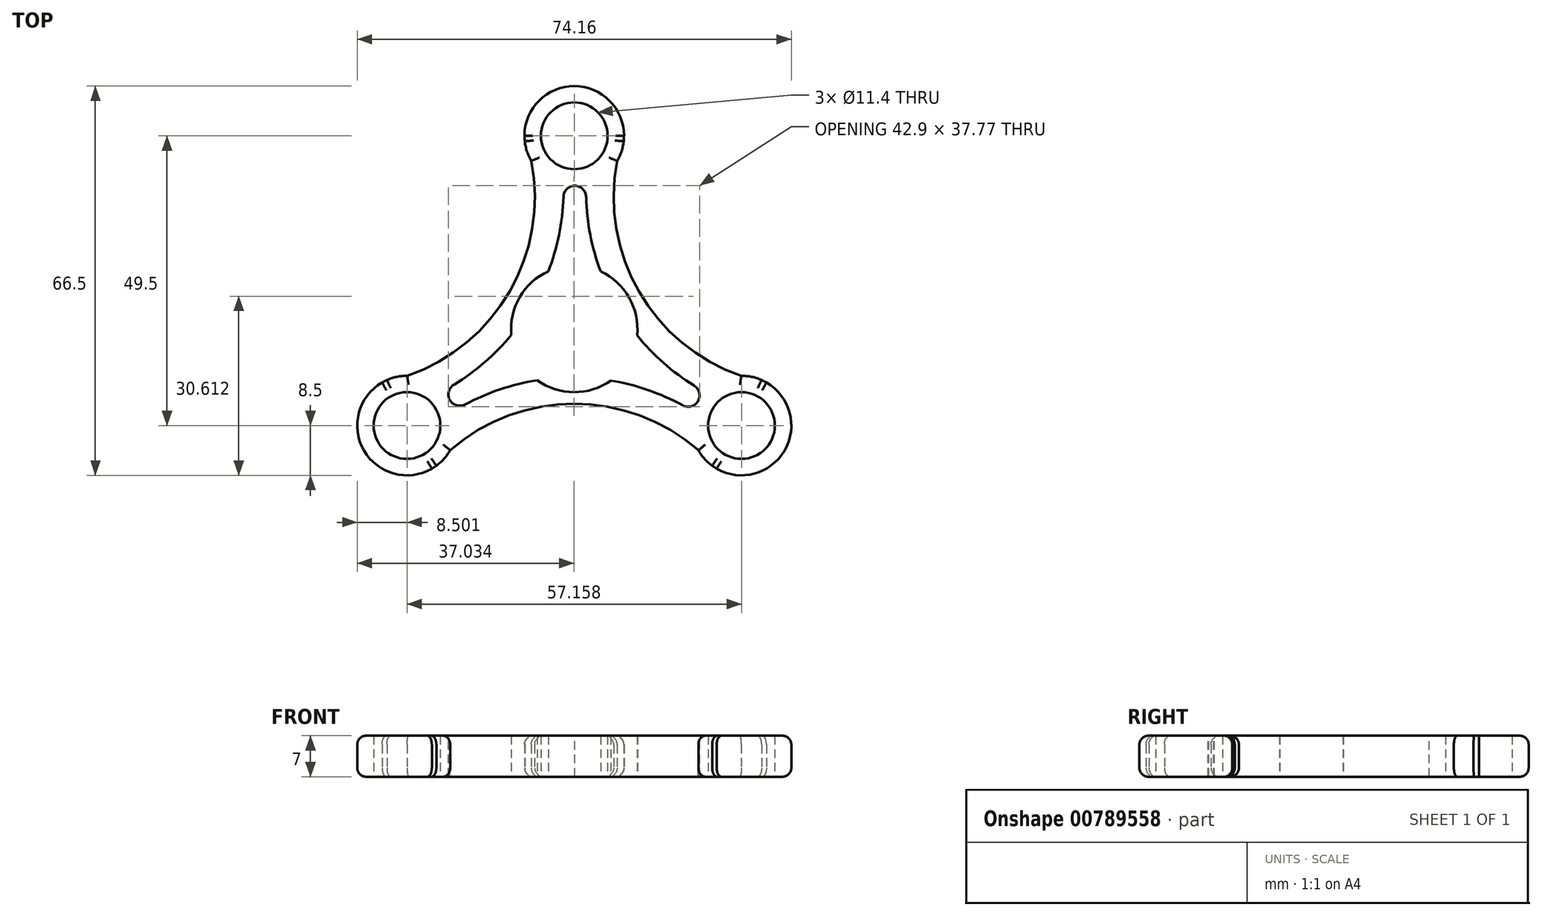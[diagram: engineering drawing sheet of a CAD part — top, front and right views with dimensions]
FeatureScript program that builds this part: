
annotation { "Feature Type Name" : "Feature", "Feature Type Description" : "" }
export const myFeature = defineFeature(function(context is Context, id is Id, definition is map)
    precondition{}
    {
        {
            var Q0;
            Q0=qCreatedBy(makeId("Top.planeOp"),FACE);
            var sketch = newSketch(context, id + "F0", { "sketchPlane" : qUnion([Q0])});
            skCircle(sketch, "E0", {"center": v(0, 0) * mm, "radius": 10.8 * mm});
            skCircle(sketch, "E1", {"center": v(0, 33) * mm, "radius": 5.7 * mm});
            skArc(sketch, "E2", {"start": v(7.35, 28.73) * mm, "mid": v(0, 41.5) * mm, "end": v(-7.35, 28.73) * mm});
            skCircle(sketch, "E3.1.0", {"center": v(-28.58, -16.5) * mm, "radius": 5.7 * mm});
            skArc(sketch, "E3.1.1", {"start": v(-28.55, -8) * mm, "mid": v(-35.94, -20.75) * mm, "end": v(-21.2, -20.73) * mm});
            skCircle(sketch, "E3.2.0", {"center": v(28.58, -16.5) * mm, "radius": 5.7 * mm});
            skArc(sketch, "E3.2.1", {"start": v(22.31, -10.76) * mm, "mid": v(21.17, -12.34) * mm, "end": v(20.41, -14.14) * mm});
            skLineSegment(sketch, "E4", {"start": v(0, 0) * mm, "end": v(28.58, -16.5) * mm, "construction": true});
            skLineSegment(sketch, "E5", {"start": v(28.58, -16.5) * mm, "end": v(38.1, 0) * mm, "construction": true});
            skArc(sketch, "E6", {"start": v(8.5, 33) * mm, "mid": v(8.47, 32.54) * mm, "end": v(8.45, 32.09) * mm});
            skArc(sketch, "E7.1.0", {"start": v(-32.83, -9.14) * mm, "mid": v(-32.42, -8.93) * mm, "end": v(-32.01, -8.72) * mm});
            skArc(sketch, "E7.2.0", {"start": v(24.33, -23.86) * mm, "mid": v(23.95, -23.6) * mm, "end": v(23.56, -23.36) * mm});
            skArc(sketch, "E8", {"start": v(2.04, 24.75) * mm, "mid": v(2.54, 17.16) * mm, "end": v(4.5, 9.81) * mm});
            skArc(sketch, "E9.trimOffspring", {"start": v(10.74, -1.1) * mm, "mid": v(16.06, -6.49) * mm, "end": v(22.31, -10.76) * mm});
            skArc(sketch, "E10.trimOffspring", {"start": v(-6.32, -8.76) * mm, "mid": v(-13.65, -10.66) * mm, "end": v(-20.47, -13.94) * mm});
            skArc(sketch, "E11.trimOffspring", {"start": v(-4.43, 9.85) * mm, "mid": v(-2.41, 17.15) * mm, "end": v(-1.84, 24.7) * mm});
            skArc(sketch, "E12.trimOffspring", {"start": v(32.01, -8.72) * mm, "mid": v(32.42, -8.93) * mm, "end": v(32.83, -9.14) * mm});
            skArc(sketch, "E13.trimOffspring", {"start": v(-23.56, -23.36) * mm, "mid": v(-23.95, -23.6) * mm, "end": v(-24.33, -23.86) * mm});
            skArc(sketch, "E14.trimOffspring", {"start": v(-8.45, 32.09) * mm, "mid": v(-8.47, 32.54) * mm, "end": v(-8.5, 33) * mm});
            skArc(sketch, "E15", {"start": v(7.35, 28.73) * mm, "mid": v(11.06, 6.38) * mm, "end": v(28.55, -8) * mm});
            skArc(sketch, "E16.1.0", {"start": v(-28.55, -8) * mm, "mid": v(-11.06, 6.38) * mm, "end": v(-7.35, 28.73) * mm});
            skArc(sketch, "E16.2.0", {"start": v(21.2, -20.73) * mm, "mid": v(0, -12.77) * mm, "end": v(-21.2, -20.73) * mm});
            skPoint(sketch, "E17.orphan", {"position": v(-2.9, 33) * mm});
            skPoint(sketch, "E18.orphan", {"position": v(3.18, 33) * mm});
            skArc(sketch, "E19.trimOffspring", {"start": v(-1.84, 24.7) * mm, "mid": v(0.1, 24.5) * mm, "end": v(2.04, 24.75) * mm});
            skPoint(sketch, "E20.orphan", {"position": v(-8.5, 33) * mm});
            skArc(sketch, "E21.trimOffspring", {"start": v(20.41, -14.14) * mm, "mid": v(13.59, -10.78) * mm, "end": v(6.25, -8.81) * mm});
            skArc(sketch, "E22.trimOffspring", {"start": v(21.2, -20.73) * mm, "mid": v(35.94, -20.75) * mm, "end": v(28.55, -8) * mm});
            skPoint(sketch, "E23.orphan", {"position": v(24.33, -23.86) * mm});
            skArc(sketch, "E24.trimOffspring", {"start": v(-22.45, -10.6) * mm, "mid": v(-16.13, -6.38) * mm, "end": v(-10.75, -1) * mm});
            skArc(sketch, "E25.trimOffspring", {"start": v(-20.47, -13.94) * mm, "mid": v(-21.27, -12.16) * mm, "end": v(-22.45, -10.6) * mm});
            skPoint(sketch, "E26.orphan", {"position": v(-32.83, -9.14) * mm});
            skPoint(sketch, "E27.orphan", {"position": v(-24.33, -23.86) * mm});
            skSolve(sketch);
        }
        {
            var Q0;
            Q0=makeQuery(id+"F0.imprint","IMPRINT",FACE,{"disambiguationData":[TD([[makeQuery(id+"F0.imprint","IMPRINT",EDGE,{"derivedFrom":sQuery(id+"F0.wireOp",EDGE,"E1")}),-1.0]])]});
            extrude(context, id + "F1", {"entities" : qUnion([Q0]), "depth" : 7 * mm, "offsetDistance" : 25 * mm});
        }
        {
            var Q0;
            Q0=makeQuery(id+"F1.opExtrude","SWEPT_EDGE",EDGE,{"disambiguationData":[OSD([sQuery(id+"F0.wireOp",EDGE,"E11.trimOffspring"),sQuery(id+"F0.wireOp",EDGE,"E19.trimOffspring")])]});
            var Q1;
            Q1=makeQuery(id+"F1.opExtrude","SWEPT_EDGE",EDGE,{"disambiguationData":[OSD([sQuery(id+"F0.wireOp",EDGE,"E8"),sQuery(id+"F0.wireOp",EDGE,"E19.trimOffspring")])]});
            var Q2;
            Q2=makeQuery(id+"F1.opExtrude","SWEPT_EDGE",EDGE,{"disambiguationData":[OSD([sQuery(id+"F0.wireOp",EDGE,"E3.2.1"),sQuery(id+"F0.wireOp",EDGE,"E9.trimOffspring")])]});
            var Q3;
            Q3=makeQuery(id+"F1.opExtrude","SWEPT_EDGE",EDGE,{"disambiguationData":[OSD([sQuery(id+"F0.wireOp",EDGE,"E3.2.1"),sQuery(id+"F0.wireOp",EDGE,"E21.trimOffspring")])]});
            var Q4;
            Q4=makeQuery(id+"F1.opExtrude","SWEPT_EDGE",EDGE,{"disambiguationData":[OSD([sQuery(id+"F0.wireOp",EDGE,"E10.trimOffspring"),sQuery(id+"F0.wireOp",EDGE,"E25.trimOffspring")])]});
            var Q5;
            Q5=makeQuery(id+"F1.opExtrude","SWEPT_EDGE",EDGE,{"disambiguationData":[OSD([sQuery(id+"F0.wireOp",EDGE,"E24.trimOffspring"),sQuery(id+"F0.wireOp",EDGE,"E25.trimOffspring")])]});
            fillet(context, id + "F2", {"entities" : qUnion([Q0, Q1, Q2, Q3, Q4, Q5]), "radius" : 2 * mm, "tangentPropagation" : true, "allowEdgeOverflow" : false});
        }
        {
            var Q0;
            Q0=makeQuery(id+"F1.opExtrude","CAP_EDGE",EDGE,{"disambiguationData":[OSD([sQuery(id+"F0.wireOp",EDGE,"E16.2.0")])],"isStart":false});
            var Q1;
            Q1=makeQuery(id+"F1.opExtrude","CAP_EDGE",EDGE,{"disambiguationData":[OSD([sQuery(id+"F0.wireOp",EDGE,"E15")])],"isStart":false});
            var Q2;
            Q2=makeQuery(id+"F1.opExtrude","CAP_EDGE",EDGE,{"disambiguationData":[OSD([sQuery(id+"F0.wireOp",EDGE,"E16.1.0")])],"isStart":false});
            var Q3;
            Q3=makeQuery(id+"F1.opExtrude","CAP_EDGE",EDGE,{"disambiguationData":[OSD([sQuery(id+"F0.wireOp",EDGE,"E16.2.0")])],"isStart":true});
            var Q4;
            Q4=makeQuery(id+"F1.opExtrude","CAP_EDGE",EDGE,{"disambiguationData":[OSD([sQuery(id+"F0.wireOp",EDGE,"E15")])],"isStart":true});
            var Q5;
            Q5=makeQuery(id+"F1.opExtrude","CAP_EDGE",EDGE,{"disambiguationData":[OSD([sQuery(id+"F0.wireOp",EDGE,"E16.1.0")])],"isStart":true});
            var Q6;
            {var subQ0=sQuery(id+"F0.wireOp",EDGE,"E3.1.1");Q6=makeQuery(id+"F1.opExtrude","CAP_EDGE",EDGE,{"disambiguationData":[OSD([subQ0]),TDD([makeQuery(id+"F0.imprint","IMPRINT",EDGE,{"disambiguationData":[TD([[makeQuery(id+"F0.imprint","INTERSECT",VERTEX,{"disambiguationData":[OD(0.0)],"derivedFrom":[subQ0,sQuery(id+"F0.wireOp",EDGE,"E7.1.0")]}),-1.0]])],"derivedFrom":subQ0})])],"isStart":true});}
            var Q7;
            {var subQ0=sQuery(id+"F0.wireOp",EDGE,"E3.1.1");Q7=makeQuery(id+"F1.opExtrude","CAP_EDGE",EDGE,{"disambiguationData":[OSD([subQ0]),TDD([makeQuery(id+"F0.imprint","IMPRINT",EDGE,{"disambiguationData":[TD([[makeQuery(id+"F0.imprint","INTERSECT",VERTEX,{"derivedFrom":[subQ0,sQuery(id+"F0.wireOp",EDGE,"E16.1.0")]}),-1.0]])],"derivedFrom":subQ0})])],"isStart":true});}
            var Q8;
            Q8=makeQuery(id+"F1.opExtrude","CAP_EDGE",EDGE,{"disambiguationData":[OSD([sQuery(id+"F0.wireOp",EDGE,"E7.1.0")])],"isStart":true});
            var Q9;
            {var subQ0=sQuery(id+"F0.wireOp",EDGE,"E3.1.1");Q9=makeQuery(id+"F1.opExtrude","CAP_EDGE",EDGE,{"disambiguationData":[OSD([subQ0]),TDD([makeQuery(id+"F0.imprint","IMPRINT",EDGE,{"disambiguationData":[TD([[makeQuery(id+"F0.imprint","INTERSECT",VERTEX,{"derivedFrom":[subQ0,sQuery(id+"F0.wireOp",EDGE,"E16.2.0")]}),1.0]])],"derivedFrom":subQ0})])],"isStart":true});}
            var Q10;
            Q10=makeQuery(id+"F1.opExtrude","CAP_EDGE",EDGE,{"disambiguationData":[OSD([sQuery(id+"F0.wireOp",EDGE,"E13.trimOffspring")])],"isStart":true});
            var Q11;
            {var subQ0=sQuery(id+"F0.wireOp",EDGE,"E22.trimOffspring");Q11=makeQuery(id+"F1.opExtrude","CAP_EDGE",EDGE,{"disambiguationData":[OSD([subQ0]),TDD([makeQuery(id+"F0.imprint","IMPRINT",EDGE,{"disambiguationData":[TD([[makeQuery(id+"F0.imprint","INTERSECT",VERTEX,{"disambiguationData":[OD(0.0)],"derivedFrom":[sQuery(id+"F0.wireOp",EDGE,"E12.trimOffspring"),subQ0]}),-1.0]])],"derivedFrom":subQ0})])],"isStart":true});}
            var Q12;
            Q12=makeQuery(id+"F1.opExtrude","CAP_EDGE",EDGE,{"disambiguationData":[OSD([sQuery(id+"F0.wireOp",EDGE,"E12.trimOffspring")])],"isStart":true});
            var Q13;
            {var subQ0=sQuery(id+"F0.wireOp",EDGE,"E22.trimOffspring");Q13=makeQuery(id+"F1.opExtrude","CAP_EDGE",EDGE,{"disambiguationData":[OSD([subQ0]),TDD([makeQuery(id+"F0.imprint","IMPRINT",EDGE,{"disambiguationData":[TD([[makeQuery(id+"F0.imprint","INTERSECT",VERTEX,{"disambiguationData":[OD(0.0)],"derivedFrom":[sQuery(id+"F0.wireOp",EDGE,"E7.2.0"),subQ0]}),-1.0]])],"derivedFrom":subQ0})])],"isStart":true});}
            var Q14;
            Q14=makeQuery(id+"F1.opExtrude","CAP_EDGE",EDGE,{"disambiguationData":[OSD([sQuery(id+"F0.wireOp",EDGE,"E7.2.0")])],"isStart":true});
            var Q15;
            {var subQ0=sQuery(id+"F0.wireOp",EDGE,"E22.trimOffspring");Q15=makeQuery(id+"F1.opExtrude","CAP_EDGE",EDGE,{"disambiguationData":[OSD([subQ0]),TDD([makeQuery(id+"F0.imprint","IMPRINT",EDGE,{"disambiguationData":[TD([[makeQuery(id+"F0.imprint","INTERSECT",VERTEX,{"disambiguationData":[OD(1.0)],"derivedFrom":[sQuery(id+"F0.wireOp",EDGE,"E7.2.0"),subQ0]}),1.0]])],"derivedFrom":subQ0})])],"isStart":true});}
            var Q16;
            {var subQ0=sQuery(id+"F0.wireOp",EDGE,"E2");Q16=makeQuery(id+"F1.opExtrude","CAP_EDGE",EDGE,{"disambiguationData":[OSD([subQ0]),TDD([makeQuery(id+"F0.imprint","IMPRINT",EDGE,{"disambiguationData":[TD([[makeQuery(id+"F0.imprint","INTERSECT",VERTEX,{"derivedFrom":[subQ0,sQuery(id+"F0.wireOp",EDGE,"E16.1.0")]}),1.0]])],"derivedFrom":subQ0})])],"isStart":true});}
            var Q17;
            Q17=makeQuery(id+"F1.opExtrude","CAP_EDGE",EDGE,{"disambiguationData":[OSD([sQuery(id+"F0.wireOp",EDGE,"E14.trimOffspring")])],"isStart":true});
            var Q18;
            {var subQ0=sQuery(id+"F0.wireOp",EDGE,"E2");Q18=makeQuery(id+"F1.opExtrude","CAP_EDGE",EDGE,{"disambiguationData":[OSD([subQ0]),TDD([makeQuery(id+"F0.imprint","IMPRINT",EDGE,{"disambiguationData":[TD([[makeQuery(id+"F0.imprint","INTERSECT",VERTEX,{"disambiguationData":[OD(0.0)],"derivedFrom":[subQ0,sQuery(id+"F0.wireOp",EDGE,"E6")]}),-1.0]])],"derivedFrom":subQ0})])],"isStart":true});}
            var Q19;
            {var subQ0=sQuery(id+"F0.wireOp",EDGE,"E2");Q19=makeQuery(id+"F1.opExtrude","CAP_EDGE",EDGE,{"disambiguationData":[OSD([subQ0]),TDD([makeQuery(id+"F0.imprint","IMPRINT",EDGE,{"disambiguationData":[TD([[makeQuery(id+"F0.imprint","INTERSECT",VERTEX,{"derivedFrom":[subQ0,sQuery(id+"F0.wireOp",EDGE,"E15")]}),-1.0]])],"derivedFrom":subQ0})])],"isStart":true});}
            var Q20;
            Q20=makeQuery(id+"F1.opExtrude","CAP_EDGE",EDGE,{"disambiguationData":[OSD([sQuery(id+"F0.wireOp",EDGE,"E6")])],"isStart":true});
            var Q21;
            {var subQ0=sQuery(id+"F0.wireOp",EDGE,"E2");Q21=makeQuery(id+"F1.opExtrude","CAP_EDGE",EDGE,{"disambiguationData":[OSD([subQ0]),TDD([makeQuery(id+"F0.imprint","IMPRINT",EDGE,{"disambiguationData":[TD([[makeQuery(id+"F0.imprint","INTERSECT",VERTEX,{"derivedFrom":[subQ0,sQuery(id+"F0.wireOp",EDGE,"E16.1.0")]}),1.0]])],"derivedFrom":subQ0})])],"isStart":false});}
            var Q22;
            Q22=makeQuery(id+"F1.opExtrude","CAP_EDGE",EDGE,{"disambiguationData":[OSD([sQuery(id+"F0.wireOp",EDGE,"E14.trimOffspring")])],"isStart":false});
            var Q23;
            {var subQ0=sQuery(id+"F0.wireOp",EDGE,"E2");Q23=makeQuery(id+"F1.opExtrude","CAP_EDGE",EDGE,{"disambiguationData":[OSD([subQ0]),TDD([makeQuery(id+"F0.imprint","IMPRINT",EDGE,{"disambiguationData":[TD([[makeQuery(id+"F0.imprint","INTERSECT",VERTEX,{"disambiguationData":[OD(0.0)],"derivedFrom":[subQ0,sQuery(id+"F0.wireOp",EDGE,"E6")]}),-1.0]])],"derivedFrom":subQ0})])],"isStart":false});}
            var Q24;
            {var subQ0=sQuery(id+"F0.wireOp",EDGE,"E2");Q24=makeQuery(id+"F1.opExtrude","CAP_EDGE",EDGE,{"disambiguationData":[OSD([subQ0]),TDD([makeQuery(id+"F0.imprint","IMPRINT",EDGE,{"disambiguationData":[TD([[makeQuery(id+"F0.imprint","INTERSECT",VERTEX,{"derivedFrom":[subQ0,sQuery(id+"F0.wireOp",EDGE,"E15")]}),-1.0]])],"derivedFrom":subQ0})])],"isStart":false});}
            var Q25;
            Q25=makeQuery(id+"F1.opExtrude","CAP_EDGE",EDGE,{"disambiguationData":[OSD([sQuery(id+"F0.wireOp",EDGE,"E6")])],"isStart":false});
            var Q26;
            {var subQ0=sQuery(id+"F0.wireOp",EDGE,"E22.trimOffspring");Q26=makeQuery(id+"F1.opExtrude","CAP_EDGE",EDGE,{"disambiguationData":[OSD([subQ0]),TDD([makeQuery(id+"F0.imprint","IMPRINT",EDGE,{"disambiguationData":[TD([[makeQuery(id+"F0.imprint","INTERSECT",VERTEX,{"disambiguationData":[OD(0.0)],"derivedFrom":[sQuery(id+"F0.wireOp",EDGE,"E12.trimOffspring"),subQ0]}),-1.0]])],"derivedFrom":subQ0})])],"isStart":false});}
            var Q27;
            Q27=makeQuery(id+"F1.opExtrude","CAP_EDGE",EDGE,{"disambiguationData":[OSD([sQuery(id+"F0.wireOp",EDGE,"E12.trimOffspring")])],"isStart":false});
            var Q28;
            {var subQ0=sQuery(id+"F0.wireOp",EDGE,"E22.trimOffspring");Q28=makeQuery(id+"F1.opExtrude","CAP_EDGE",EDGE,{"disambiguationData":[OSD([subQ0]),TDD([makeQuery(id+"F0.imprint","IMPRINT",EDGE,{"disambiguationData":[TD([[makeQuery(id+"F0.imprint","INTERSECT",VERTEX,{"disambiguationData":[OD(0.0)],"derivedFrom":[sQuery(id+"F0.wireOp",EDGE,"E7.2.0"),subQ0]}),-1.0]])],"derivedFrom":subQ0})])],"isStart":false});}
            var Q29;
            Q29=makeQuery(id+"F1.opExtrude","CAP_EDGE",EDGE,{"disambiguationData":[OSD([sQuery(id+"F0.wireOp",EDGE,"E7.2.0")])],"isStart":false});
            var Q30;
            {var subQ0=sQuery(id+"F0.wireOp",EDGE,"E22.trimOffspring");Q30=makeQuery(id+"F1.opExtrude","CAP_EDGE",EDGE,{"disambiguationData":[OSD([subQ0]),TDD([makeQuery(id+"F0.imprint","IMPRINT",EDGE,{"disambiguationData":[TD([[makeQuery(id+"F0.imprint","INTERSECT",VERTEX,{"disambiguationData":[OD(1.0)],"derivedFrom":[sQuery(id+"F0.wireOp",EDGE,"E7.2.0"),subQ0]}),1.0]])],"derivedFrom":subQ0})])],"isStart":false});}
            var Q31;
            {var subQ0=sQuery(id+"F0.wireOp",EDGE,"E3.1.1");Q31=makeQuery(id+"F1.opExtrude","CAP_EDGE",EDGE,{"disambiguationData":[OSD([subQ0]),TDD([makeQuery(id+"F0.imprint","IMPRINT",EDGE,{"disambiguationData":[TD([[makeQuery(id+"F0.imprint","INTERSECT",VERTEX,{"derivedFrom":[subQ0,sQuery(id+"F0.wireOp",EDGE,"E16.2.0")]}),1.0]])],"derivedFrom":subQ0})])],"isStart":false});}
            var Q32;
            Q32=makeQuery(id+"F1.opExtrude","CAP_EDGE",EDGE,{"disambiguationData":[OSD([sQuery(id+"F0.wireOp",EDGE,"E13.trimOffspring")])],"isStart":false});
            var Q33;
            {var subQ0=sQuery(id+"F0.wireOp",EDGE,"E3.1.1");Q33=makeQuery(id+"F1.opExtrude","CAP_EDGE",EDGE,{"disambiguationData":[OSD([subQ0]),TDD([makeQuery(id+"F0.imprint","IMPRINT",EDGE,{"disambiguationData":[TD([[makeQuery(id+"F0.imprint","INTERSECT",VERTEX,{"disambiguationData":[OD(0.0)],"derivedFrom":[subQ0,sQuery(id+"F0.wireOp",EDGE,"E7.1.0")]}),-1.0]])],"derivedFrom":subQ0})])],"isStart":false});}
            var Q34;
            {var subQ0=sQuery(id+"F0.wireOp",EDGE,"E3.1.1");Q34=makeQuery(id+"F1.opExtrude","CAP_EDGE",EDGE,{"disambiguationData":[OSD([subQ0]),TDD([makeQuery(id+"F0.imprint","IMPRINT",EDGE,{"disambiguationData":[TD([[makeQuery(id+"F0.imprint","INTERSECT",VERTEX,{"derivedFrom":[subQ0,sQuery(id+"F0.wireOp",EDGE,"E16.1.0")]}),-1.0]])],"derivedFrom":subQ0})])],"isStart":false});}
            var Q35;
            Q35=makeQuery(id+"F1.opExtrude","CAP_EDGE",EDGE,{"disambiguationData":[OSD([sQuery(id+"F0.wireOp",EDGE,"E7.1.0")])],"isStart":false});
            fillet(context, id + "F3", {"entities" : qUnion([Q0, Q1, Q2, Q3, Q4, Q5, Q6, Q7, Q8, Q9, Q10, Q11, Q12, Q13, Q14, Q15, Q16, Q17, Q18, Q19, Q20, Q21, Q22, Q23, Q24, Q25, Q26, Q27, Q28, Q29, Q30, Q31, Q32, Q33, Q34, Q35]), "radius" : 1.5 * mm, "tangentPropagation" : true, "allowEdgeOverflow" : false});
        }
    });
